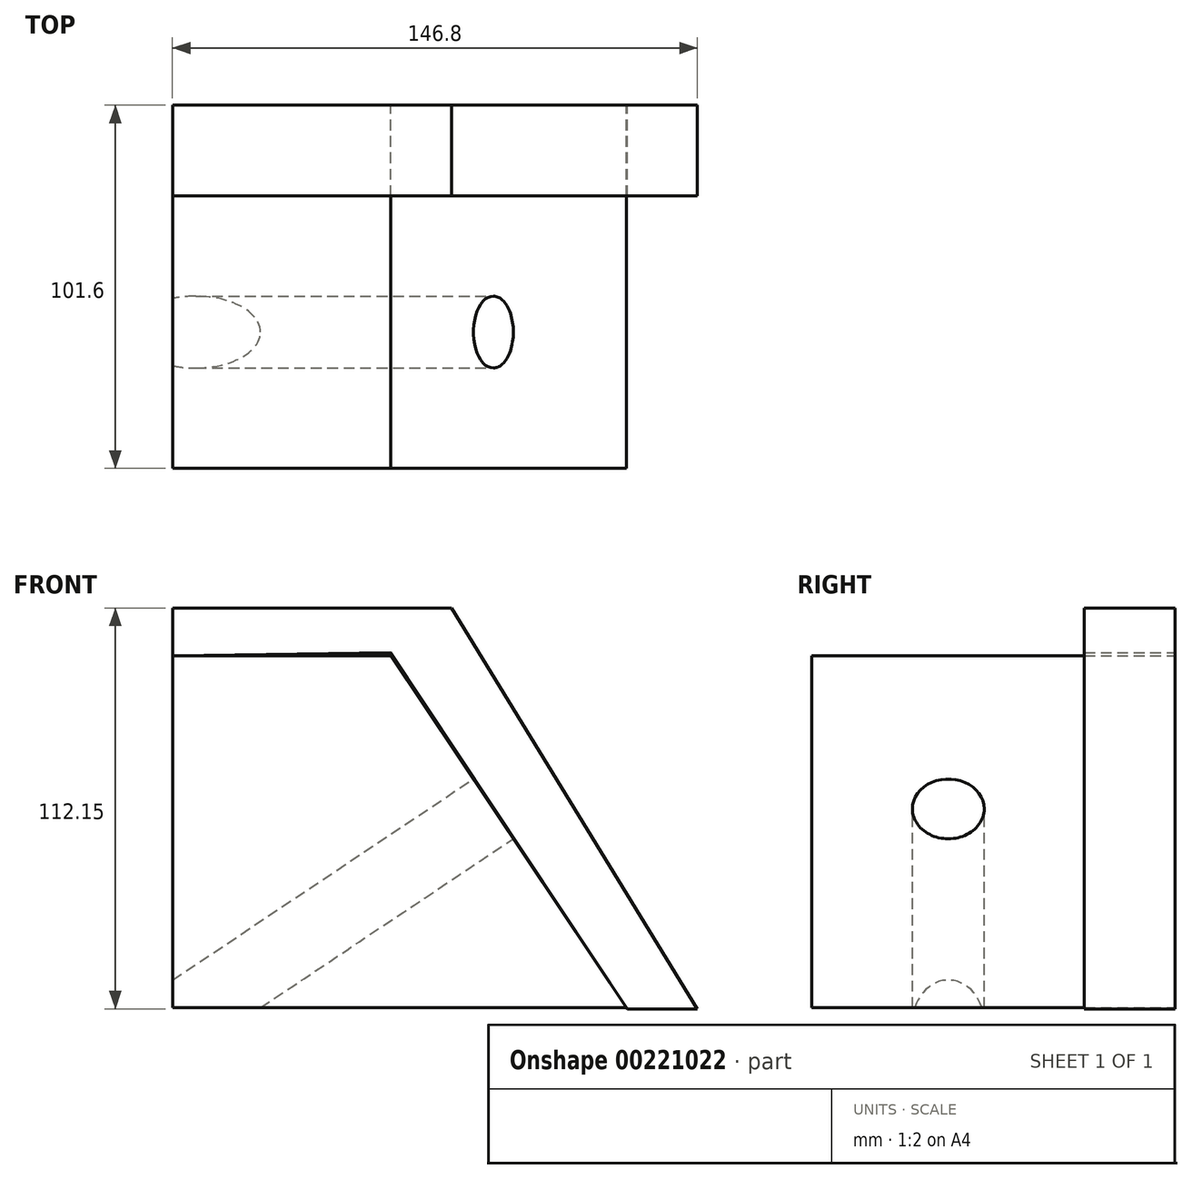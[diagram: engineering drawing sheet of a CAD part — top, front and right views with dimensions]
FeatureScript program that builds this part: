
annotation { "Feature Type Name" : "Feature", "Feature Type Description" : "" }
export const myFeature = defineFeature(function(context is Context, id is Id, definition is map)
    precondition{}
    {
        {
            var Q0;
            Q0=qCreatedBy(makeId("Front.planeOp"),FACE);
            var sketch = newSketch(context, id + "F0", { "sketchPlane" : qUnion([Q0])});
            skLineSegment(sketch, "E0", {"start": v(-61.05, 31.66) * mm, "end": v(-61.05, -66.87) * mm});
            skLineSegment(sketch, "E1", {"start": v(-61.05, -66.87) * mm, "end": v(65.87, -66.87) * mm});
            skLineSegment(sketch, "E2", {"start": v(65.87, -66.87) * mm, "end": v(0, 31.66) * mm});
            skLineSegment(sketch, "E3", {"start": v(0, 31.66) * mm, "end": v(-61.05, 31.66) * mm});
            skSolve(sketch);
        }
        {
            var Q0;
            Q0 = qSketchRegion(id + "F0", true);
            extrude(context, id + "F1", {"entities" : qUnion([Q0]), "depth" : 101.6 * mm});
        }
        {
            var Q0;
            Q0=qCreatedBy(makeId("Front.planeOp"),FACE);
            var sketch = newSketch(context, id + "F2", { "sketchPlane" : qUnion([Q0])});
            skLineSegment(sketch, "E4", {"start": v(-61.05, 31.66) * mm, "end": v(-61.05, 45) * mm});
            skLineSegment(sketch, "E5", {"start": v(-61.05, 45) * mm, "end": v(17.04, 45) * mm});
            skLineSegment(sketch, "E6", {"start": v(17.04, 45) * mm, "end": v(85.75, -67.15) * mm});
            skLineSegment(sketch, "E7", {"start": v(85.75, -67.15) * mm, "end": v(66.16, -67.15) * mm});
            skLineSegment(sketch, "E8", {"start": v(66.16, -67.15) * mm, "end": v(0, 32.51) * mm});
            skLineSegment(sketch, "E9", {"start": v(0, 32.51) * mm, "end": v(-61.05, 31.66) * mm});
            skSolve(sketch);
        }
        {
            var Q0;
            Q0 = qSketchRegion(id + "F2", true);
            extrude(context, id + "F3", {"entities" : qUnion([Q0]), "depth" : 25.4 * mm});
        }
        {
            var Q0;
            Q0=makeQuery(id+"F1.opExtrude","SWEPT_FACE",FACE,{"disambiguationData":[OSD([sQuery(id+"F0.wireOp",EDGE,"E2")])]});
            var sketch = newSketch(context, id + "F4", { "sketchPlane" : qUnion([Q0])});
            skCircle(sketch, "E10", {"center": v(-63.45, -25.26) * mm, "radius": 10.05 * mm});
            skSolve(sketch);
        }
        {
            var Q0;
            Q0 = qSketchRegion(id + "F4", true);
            extrude(context, id + "F5", {"entities" : qUnion([Q0]), "operationType" : NewBodyOperationType.REMOVE, "endBound" : BoundingType.THROUGH_ALL, "oppositeDirection" : true, "depth" : 25.4 * mm});
        }
    });
